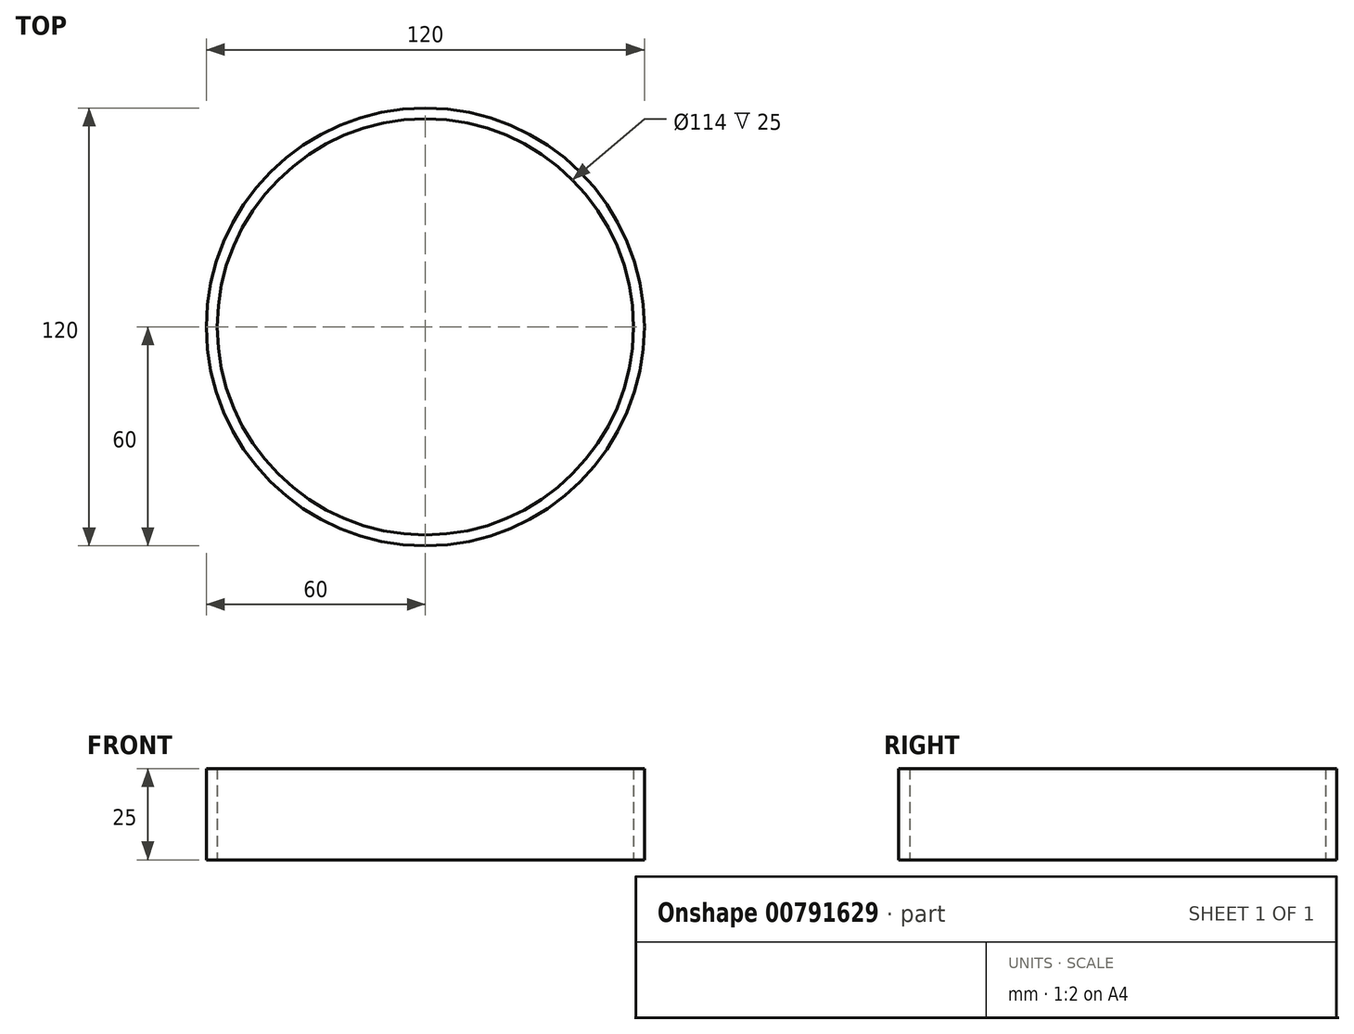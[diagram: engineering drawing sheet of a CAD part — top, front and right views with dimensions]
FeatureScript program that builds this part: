
annotation { "Feature Type Name" : "Feature", "Feature Type Description" : "" }
export const myFeature = defineFeature(function(context is Context, id is Id, definition is map)
    precondition{}
    {
        {
            var Q0;
            Q0=qCreatedBy(makeId("Top.planeOp"),FACE);
            var sketch = newSketch(context, id + "F0", { "sketchPlane" : qUnion([Q0])});
            skCircle(sketch, "E0", {"center": v(0, 0) * mm, "radius": 60 * mm});
            skCircle(sketch, "E1.0", {"center": v(0, 0) * mm, "radius": 57 * mm});
            skSolve(sketch);
        }
        {
            var Q0;
            Q0=makeQuery(id+"F0.imprint","IMPRINT",FACE,{"disambiguationData":[TD([[makeQuery(id+"F0.imprint","IMPRINT",EDGE,{"derivedFrom":sQuery(id+"F0.wireOp",EDGE,"E0")}),1.0]])]});
            extrude(context, id + "F1", {"entities" : qUnion([Q0]), "depth" : 25 * mm, "offsetDistance" : 25 * mm});
        }
    });
